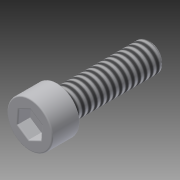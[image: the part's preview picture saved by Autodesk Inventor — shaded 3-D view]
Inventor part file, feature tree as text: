
AUTODESK INVENTOR PART (.ipt)
format: ipt  version: 2014 (Build 180170000, 170)  size: 133,120 bytes
history: native  units: in
note: dims shown in document units (in); Inventor stores cm internally (conversion verified against a paired STEP export)
features: extrude x3, fillet x3, sketch x3, projected_geometry x2, thread x1, chamfer x1
ambient origin geometry x8: Origin, YZ Plane, XZ Plane, XY Plane, X Axis, Y Axis, Z Axis, Center Point
bodies: Solid1 (feature_tree)
feature tree (13):
  extrude  "Extrusion1"  TaperAngle=0.0deg  [1 undecoded]
  extrude  "Extrusion2"  Depth=1.0in TaperAngle=0.0deg
  extrude  "Extrusion3"  Depth=0.005in
  thread  "Thread1"  [1 undecoded]
  chamfer  "Chamfer1"  Distance=0.005in
  fillet  "Fillet1"  [1 undecoded]
  fillet  "Fillet2"  [1 undecoded]
  fillet  "Fillet3"  [1 undecoded]
  sketch  "Sketch1"  dims[d2=0.0in d5=0.0in]
  sketch  "Sketch2"  dims[d8=0.0in d9=1.0in d10=0.0in]
  projected_geometry  "Projected Loop1"
  sketch  "Sketch3"  dims[d11=0.01in d12=0.125in d13=45.0deg d14=0.005in d15=0.005in d16=0.005in]
  projected_geometry  "Projected Loop2"
note: 5 required parameter values undecoded (feature->parameter linkage not recoverable at this tier; creation-order binding heuristic only, values carry confidence <= 0.55)
